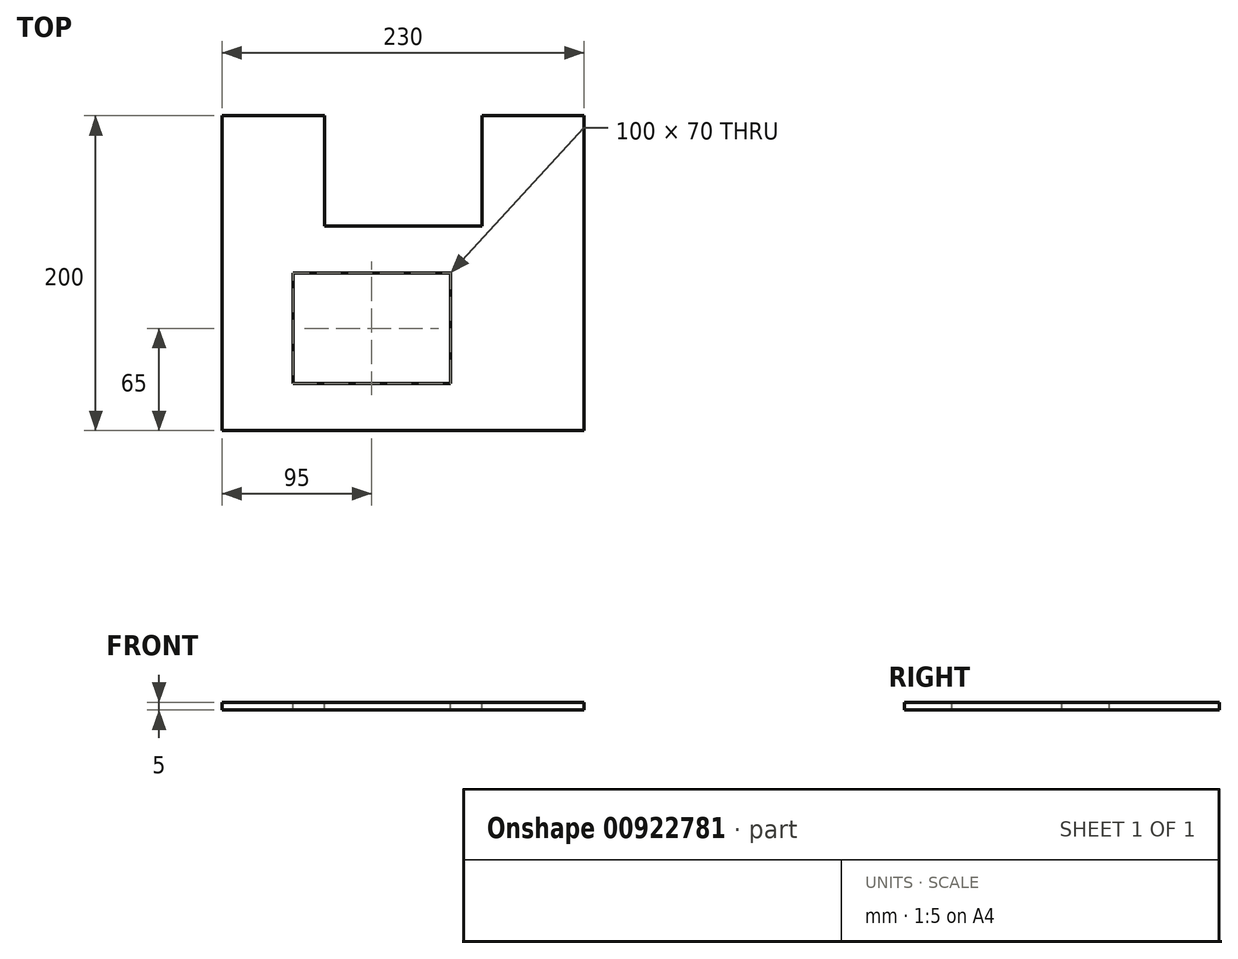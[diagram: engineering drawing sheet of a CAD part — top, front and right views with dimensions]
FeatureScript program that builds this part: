
annotation { "Feature Type Name" : "Feature", "Feature Type Description" : "" }
export const myFeature = defineFeature(function(context is Context, id is Id, definition is map)
    precondition{}
    {
        {
            var Q0;
            Q0=qCreatedBy(makeId("Top.planeOp"),FACE);
            var sketch = newSketch(context, id + "F0", { "sketchPlane" : qUnion([Q0])});
            skLineSegment(sketch, "E0.bottom", {"start": v(-115, 100) * mm, "end": v(115, 100) * mm});
            skLineSegment(sketch, "E0.top", {"start": v(-115, -100) * mm, "end": v(115, -100) * mm});
            skLineSegment(sketch, "E0.left", {"start": v(-115, 100) * mm, "end": v(-115, -100) * mm});
            skLineSegment(sketch, "E0.right", {"start": v(115, 100) * mm, "end": v(115, -100) * mm});
            skSolve(sketch);
        }
        {
            var Q0;
            Q0=makeQuery(id+"F0.imprint","IMPRINT",FACE,{"disambiguationData":[TD([[makeQuery(id+"F0.imprint","IMPRINT",EDGE,{"derivedFrom":sQuery(id+"F0.wireOp",EDGE,"E0.bottom")}),-1.0]])]});
            extrude(context, id + "F1", {"entities" : qUnion([Q0]), "depth" : 5 * mm, "offsetDistance" : 25 * mm});
        }
        {
            var Q0;
            Q0=makeQuery(id+"F1.opExtrude","CAP_FACE",FACE,{"disambiguationData":[OSD([sQuery(id+"F0.wireOp",EDGE,"E0.bottom"),sQuery(id+"F0.wireOp",EDGE,"E0.top"),sQuery(id+"F0.wireOp",EDGE,"E0.left"),sQuery(id+"F0.wireOp",EDGE,"E0.right")])],"isStart":false});
            var sketch = newSketch(context, id + "F2", { "sketchPlane" : qUnion([Q0])});
            skLineSegment(sketch, "E1.bottom", {"start": v(-50, 100) * mm, "end": v(50, 100) * mm});
            skLineSegment(sketch, "E1.top", {"start": v(-50, 30) * mm, "end": v(50, 30) * mm});
            skLineSegment(sketch, "E1.left", {"start": v(-50, 100) * mm, "end": v(-50, 30) * mm});
            skLineSegment(sketch, "E1.right", {"start": v(50, 100) * mm, "end": v(50, 30) * mm});
            skLineSegment(sketch, "E2.bottom", {"start": v(30, -70) * mm, "end": v(-70, -70) * mm});
            skLineSegment(sketch, "E2.top", {"start": v(30, 0) * mm, "end": v(-70, 0) * mm});
            skLineSegment(sketch, "E2.left", {"start": v(30, -70) * mm, "end": v(30, 0) * mm});
            skLineSegment(sketch, "E2.right", {"start": v(-70, -70) * mm, "end": v(-70, 0) * mm});
            skPoint(sketch, "E2.middle", {"position": v(0, -35) * mm});
            skSolve(sketch);
        }
        {
            var Q0;
            Q0=makeQuery(id+"F2.imprint","IMPRINT",FACE,{"disambiguationData":[TD([[makeQuery(id+"F2.imprint","IMPRINT",EDGE,{"derivedFrom":sQuery(id+"F2.wireOp",EDGE,"E1.bottom")}),-1.0]])]});
            var Q1;
            Q1=makeQuery(id+"F2.imprint","IMPRINT",FACE,{"disambiguationData":[TD([[makeQuery(id+"F2.imprint","IMPRINT",EDGE,{"derivedFrom":sQuery(id+"F2.wireOp",EDGE,"E2.bottom")}),-1.0]])]});
            extrude(context, id + "F3", {"entities" : qUnion([Q0, Q1]), "operationType" : NewBodyOperationType.REMOVE, "oppositeDirection" : true, "depth" : 25 * mm, "offsetDistance" : 25 * mm});
        }
    });
